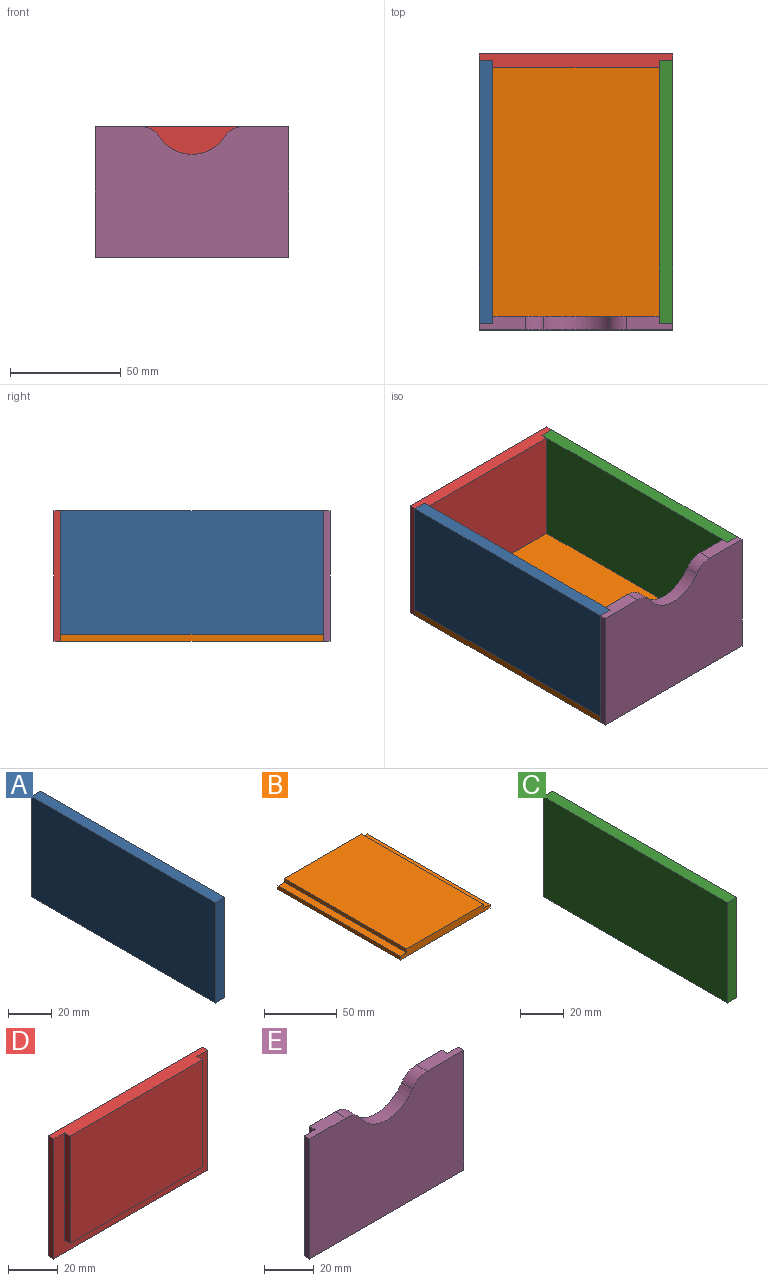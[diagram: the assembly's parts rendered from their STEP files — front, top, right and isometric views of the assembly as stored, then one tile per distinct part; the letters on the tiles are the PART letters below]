
ASSEMBLY  parts=5 mates=4
PART A: 6 faces, bbox 6.2x118.7x55.9 mm
  f0: plane 118.7x6.2mm, normal (0,0,-1), area 735.9mm2, adj f1,f3,f4,f5
  f1: plane 55.9x6.2mm, normal (0,-1,0), area 346.6mm2, adj f0,f2,f4,f5
  f2: plane 118.7x6.2mm, normal (0,0,1), area 735.9mm2, adj f1,f3,f4,f5
  f3: plane 55.9x6.2mm, normal (0,1,0), area 346.6mm2, adj f0,f2,f4,f5
  f4: plane 118.7x55.9mm, normal (1,0,0), area 6635.3mm2, adj f0,f1,f2,f3
  f5: plane 118.7x55.9mm, normal (-1,0,0), area 6635.3mm2, adj f0,f1,f2,f3
PART B: 10 faces, bbox 87.5x118.7x6.2 mm
  f0: plane 118.7x3.1mm, normal (1,0,0), area 368mm2, adj f1,f3,f5,f7
  f1: plane 87.5x6.2mm, normal (0,-1,0), area 504.1mm2, adj f0,f2,f4,f5,f6,f7,f8,f9
  f2: plane 118.7x3.1mm, normal (-1,0,0), area 368mm2, adj f1,f3,f5,f9
  f3: plane 87.5x6.2mm, normal (0,1,0), area 504.1mm2, adj f0,f2,f4,f5,f6,f7,f8,f9
  f4: plane 118.7x75.1mm, normal (0,0,1), area 8914.4mm2, adj f1,f3,f6,f8
  f5: plane 118.7x87.5mm, normal (0,0,-1), area 10386.2mm2, adj f0,f1,f2,f3
  f6: plane 118.7x3.1mm, normal (1,0,0), area 368mm2, adj f1,f3,f4,f7
  f7: plane 118.7x6.2mm, normal (0,0,1), area 735.9mm2, adj f0,f1,f3,f6
  f8: plane 118.7x3.1mm, normal (-1,0,0), area 368mm2, adj f1,f3,f4,f9
  f9: plane 118.7x6.2mm, normal (0,0,1), area 735.9mm2, adj f1,f2,f3,f8
PART C: 6 faces, bbox 6.2x118.7x55.9 mm
  f0: plane 118.7x6.2mm, normal (0,0,-1), area 735.9mm2, adj f1,f3,f4,f5
  f1: plane 55.9x6.2mm, normal (0,-1,0), area 346.6mm2, adj f0,f2,f4,f5
  f2: plane 118.7x6.2mm, normal (0,0,1), area 735.9mm2, adj f1,f3,f4,f5
  f3: plane 55.9x6.2mm, normal (0,1,0), area 346.6mm2, adj f0,f2,f4,f5
  f4: plane 118.7x55.9mm, normal (1,0,0), area 6635.3mm2, adj f0,f1,f2,f3
  f5: plane 118.7x55.9mm, normal (-1,0,0), area 6635.3mm2, adj f0,f1,f2,f3
PART D: 10 faces, bbox 87.5x6.2x59 mm
  f0: plane 59x3.1mm, normal (-1,0,0), area 182.9mm2, adj f1,f3,f4,f5
  f1: plane 87.5x6.2mm, normal (0,0,1), area 504.1mm2, adj f0,f2,f4,f5,f6,f7,f9
  f2: plane 59x3.1mm, normal (1,0,0), area 182.9mm2, adj f1,f3,f4,f5
  f3: plane 87.5x3.1mm, normal (0,0,-1), area 271.3mm2, adj f0,f2,f4,f5
  f4: plane 87.5x59mm, normal (0,1,0), area 5162.5mm2, adj f0,f1,f2,f3
  f5: plane 87.5x59mm, normal (0,-1,0), area 1197.2mm2, adj f0,f1,f2,f3,f6,f7,f8
  f6: plane 52.8x3.1mm, normal (1,0,0), area 163.7mm2, adj f1,f5,f8,f9
  f7: plane 52.8x3.1mm, normal (-1,0,0), area 163.7mm2, adj f1,f5,f8,f9
  f8: plane 75.1x3.1mm, normal (0,0,-1), area 232.8mm2, adj f5,f6,f7,f9
  f9: plane 75.1x52.8mm, normal (0,-1,0), area 3965.3mm2, adj f1,f6,f7,f8
PART E: 14 faces, bbox 87.5x6.2x59 mm
  f0: plane 20.7x6.2mm, normal (0,0,1), area 109.1mm2, adj f2,f3,f6,f9,f10,f12
  f1: plane 20.7x6.2mm, normal (0,0,1), area 109.1mm2, adj f2,f5,f6,f7,f10,f13
  f2: plane 75.1x52.8mm, normal (0,1,0), area 3645.1mm2, adj f0,f1,f7,f8,f9,f11,f12,f13
  f3: plane 59x3.1mm, normal (-1,0,0), area 182.9mm2, adj f0,f4,f6,f10
  f4: plane 87.5x3.1mm, normal (0,0,-1), area 271.2mm2, adj f3,f5,f6,f10
  f5: plane 59x3.1mm, normal (1,0,0), area 182.9mm2, adj f1,f4,f6,f10
  f6: plane 87.5x59mm, normal (0,-1,0), area 4842.3mm2, adj f0,f1,f3,f4,f5,f11,f12,f13
  f7: plane 52.8x3.1mm, normal (1,0,0), area 163.7mm2, adj f1,f2,f8,f10
  f8: plane 75.1x3.1mm, normal (0,0,-1), area 232.8mm2, adj f2,f7,f9,f10
  f9: plane 52.8x3.1mm, normal (-1,0,0), area 163.7mm2, adj f0,f2,f8,f10
  f10: plane 87.5x59mm, normal (0,1,0), area 1197.2mm2, adj f0,f1,f3,f4,f5,f7,f8,f9
  f11: cylinder r=17.5mm len=29.34mm, axis (0,-1,0), area 215.7mm2, adj f2,f6,f12,f13
  f12: cylinder r=10mm len=8.38mm, axis (0,-1,0), area 61.6mm2, adj f0,f2,f6,f11
  f13: cylinder r=10mm len=8.38mm, axis (0,-1,0), area 61.6mm2, adj f1,f2,f6,f11
PLACE A at identity
PLACE B at identity
PLACE C at identity
PLACE D at identity
PLACE E at identity fixed
MATE fastened B.f1 <-> E.f10  axis (0,-1,0) through (87.5,-3.1,0)mm
MATE fastened A.f2 <-> D.f1  axis (0,0,1) through (6.2,115.6,59)mm
MATE fastened A.f2 <-> E.f0  axis (0,0,1) through (6.2,-3.1,59)mm
MATE fastened C.f2 <-> E.f1  axis (0,0,1) through (81.3,-3.1,59)mm
